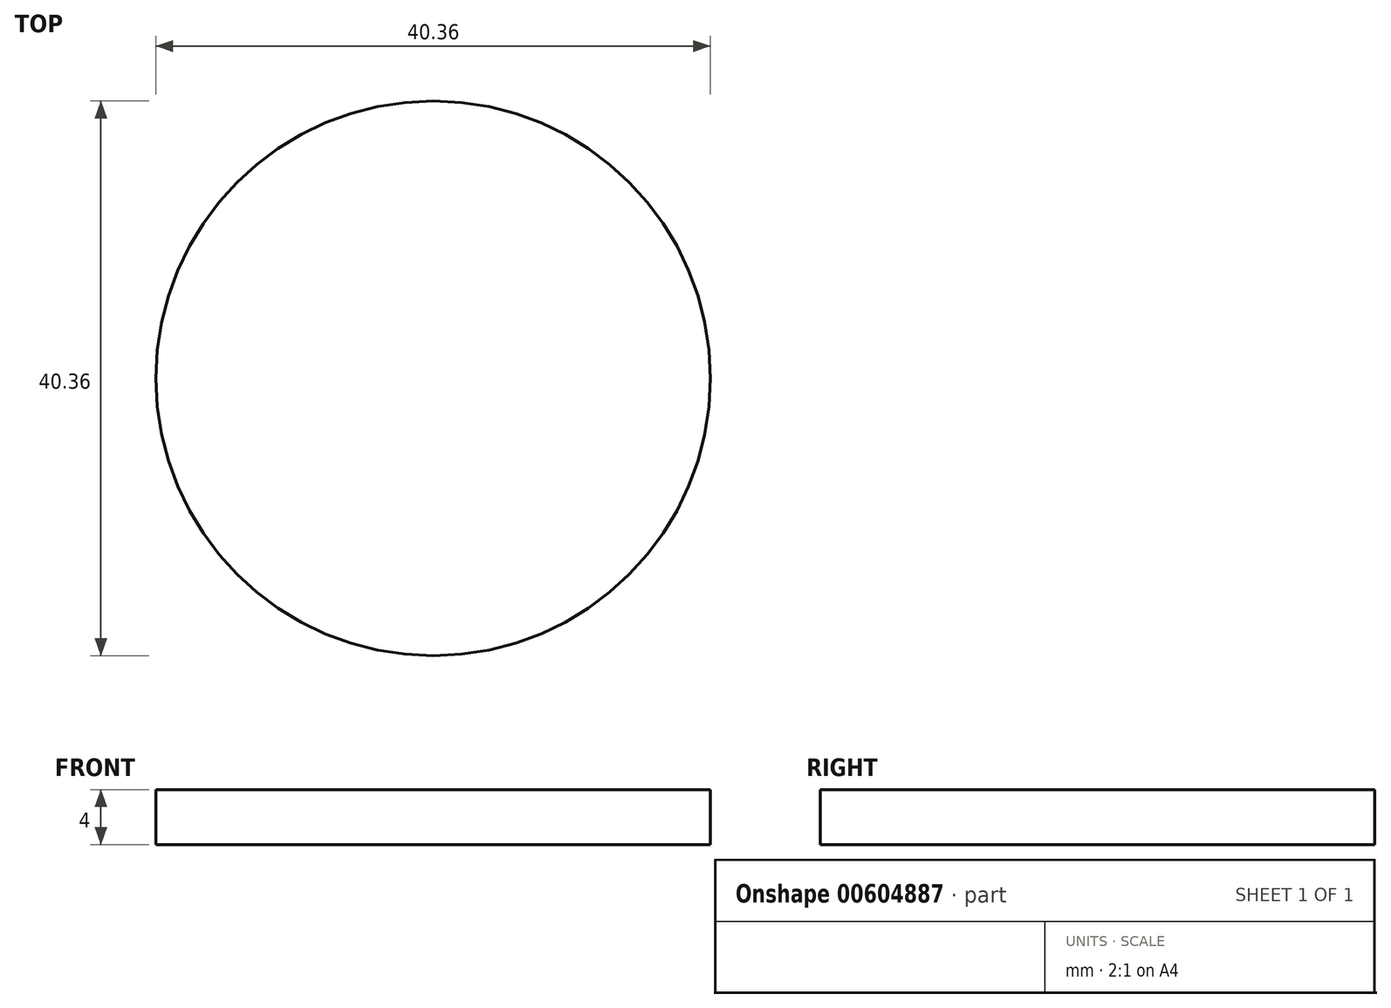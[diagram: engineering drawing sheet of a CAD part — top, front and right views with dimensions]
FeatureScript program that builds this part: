
annotation { "Feature Type Name" : "Feature", "Feature Type Description" : "" }
export const myFeature = defineFeature(function(context is Context, id is Id, definition is map)
    precondition{}
    {
        {
            var Q0;
            Q0=qCreatedBy(makeId("Top.planeOp"),FACE);
            var sketch = newSketch(context, id + "F0", { "sketchPlane" : qUnion([Q0])});
            skCircle(sketch, "E0", {"center": v(0, 0) * mm, "radius": 20.18 * mm});
            skSolve(sketch);
        }
        {
            var Q0;
            Q0=makeQuery(id+"F0.imprint","IMPRINT",FACE,{"disambiguationData":[TD([[makeQuery(id+"F0.imprint","IMPRINT",EDGE,{"derivedFrom":sQuery(id+"F0.wireOp",EDGE,"E0")}),1.0]])]});
            extrude(context, id + "F1", {"entities" : qUnion([Q0]), "depth" : 4 * mm, "offsetDistance" : 25 * mm});
        }
    });
